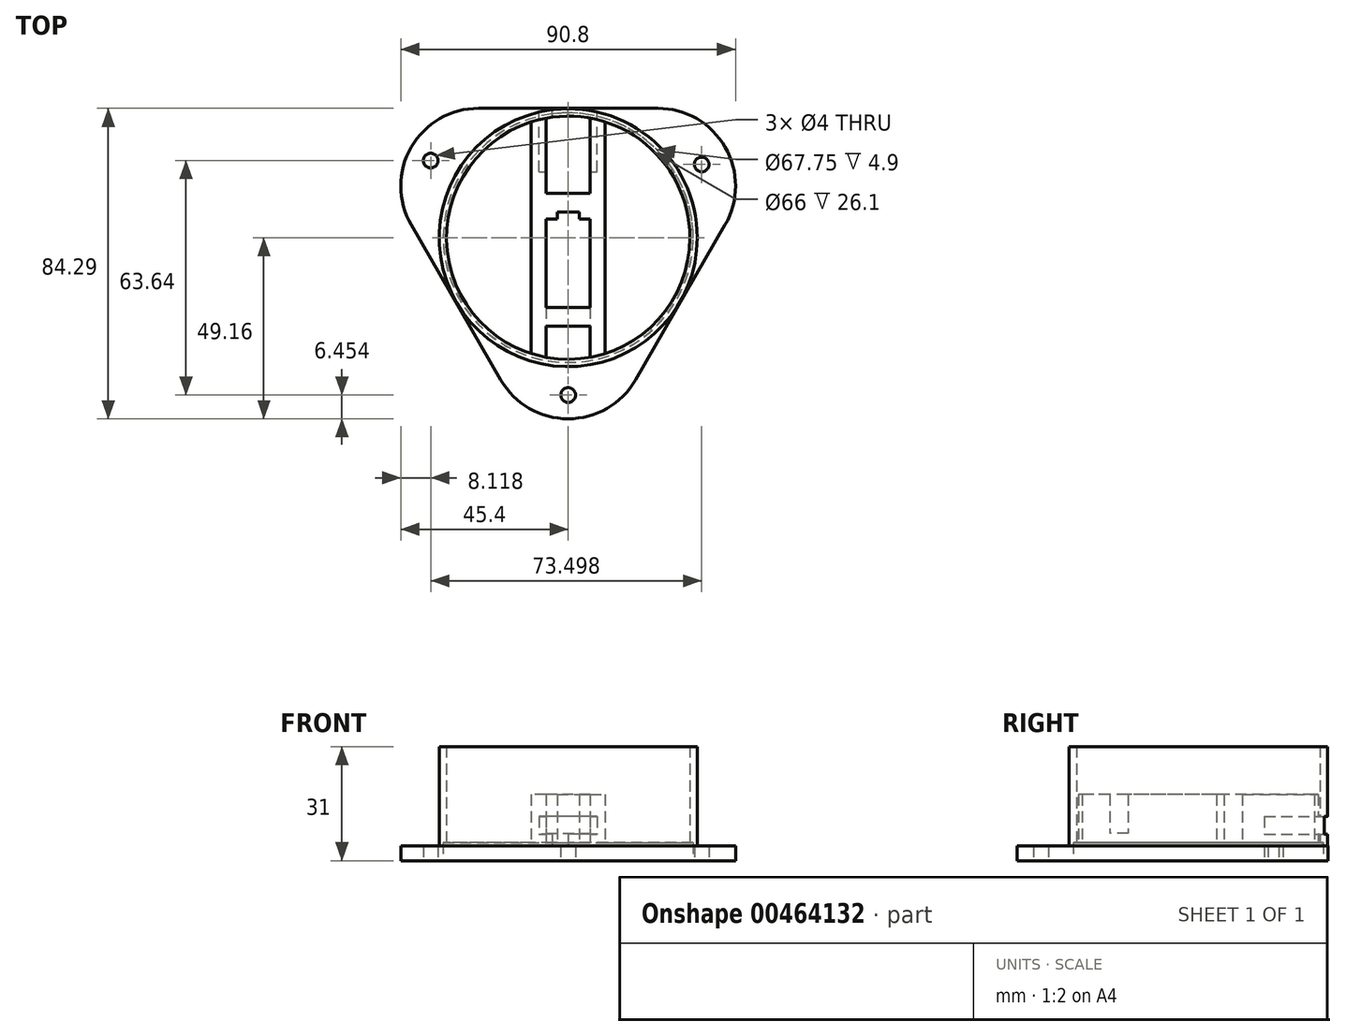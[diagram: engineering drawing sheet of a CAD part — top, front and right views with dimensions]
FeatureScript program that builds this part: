
annotation { "Feature Type Name" : "Feature", "Feature Type Description" : "" }
export const myFeature = defineFeature(function(context is Context, id is Id, definition is map)
    precondition{}
    {
        {
            var Q0;
            Q0=qCreatedBy(makeId("Top.planeOp"),FACE);
            var sketch = newSketch(context, id + "F0", { "sketchPlane" : qUnion([Q0])});
            skCircle(sketch, "E0", {"center": v(0, 0) * mm, "radius": 35 * mm});
            skCircle(sketch, "E1", {"center": v(0, 0) * mm, "radius": 33 * mm});
            skSolve(sketch);
        }
        {
            var Q0;
            Q0=qCreatedBy(makeId("Top.planeOp"),FACE);
            var sketch = newSketch(context, id + "F1", { "sketchPlane" : qUnion([Q0])});
            skPoint(sketch, "E2", {"position": v(0, -24) * mm});
            skPoint(sketch, "E3", {"position": v(0, -19) * mm});
            skPoint(sketch, "E4", {"position": v(6, -19) * mm});
            skPoint(sketch, "E5", {"position": v(-6, -19) * mm});
            skPoint(sketch, "E6", {"position": v(6, -24) * mm});
            skPoint(sketch, "E7", {"position": v(-6, -24) * mm});
            skPoint(sketch, "E8", {"position": v(10, -24) * mm});
            skLineSegment(sketch, "E9", {"start": v(10, -24) * mm, "end": v(10, -32.05) * mm});
            skLineSegment(sketch, "E10", {"start": v(6, -24) * mm, "end": v(6, -33.1) * mm});
            skPoint(sketch, "E11", {"position": v(6, 5) * mm});
            skPoint(sketch, "E12", {"position": v(3, 5) * mm});
            skPoint(sketch, "E13", {"position": v(3, 7) * mm});
            skPoint(sketch, "E14", {"position": v(3, 12) * mm});
            skPoint(sketch, "E15", {"position": v(6, 12) * mm});
            skPoint(sketch, "E16", {"position": v(10, 5) * mm});
            skPoint(sketch, "E17", {"position": v(10, 12) * mm});
            skLineSegment(sketch, "E18", {"start": v(10, -24) * mm, "end": v(10, 32.28) * mm});
            skLineSegment(sketch, "E19", {"start": v(6, 12) * mm, "end": v(6, 33.47) * mm});
            skLineSegment(sketch, "E20", {"start": v(6, 12) * mm, "end": v(3, 12) * mm});
            skLineSegment(sketch, "E21", {"start": v(3, 7) * mm, "end": v(3, 5) * mm});
            skLineSegment(sketch, "E22", {"start": v(3, 5) * mm, "end": v(6, 5) * mm});
            skLineSegment(sketch, "E23", {"start": v(6, 5) * mm, "end": v(6, -19) * mm});
            skPoint(sketch, "E24", {"position": v(0, 7) * mm});
            skPoint(sketch, "E25", {"position": v(0, 12) * mm});
            skLineSegment(sketch, "E26", {"start": v(3, 7) * mm, "end": v(0, 7) * mm});
            skLineSegment(sketch, "E27", {"start": v(3, 12) * mm, "end": v(0, 12) * mm});
            skLineSegment(sketch, "E28", {"start": v(0, -24) * mm, "end": v(6, -24) * mm});
            skLineSegment(sketch, "E29", {"start": v(0, -19) * mm, "end": v(6, -19) * mm});
            skLineSegment(sketch, "E30.MirrorCS", {"start": v(-3, 12) * mm, "end": v(0, 12) * mm});
            skLineSegment(sketch, "E31.MirrorCS", {"start": v(-6, 12) * mm, "end": v(-3, 12) * mm});
            skLineSegment(sketch, "E32.MirrorCS", {"start": v(-6, 12) * mm, "end": v(-6, 33.47) * mm});
            skLineSegment(sketch, "E33.MirrorCS", {"start": v(-10, -24) * mm, "end": v(-10, 32.28) * mm});
            skLineSegment(sketch, "E34.MirrorCS", {"start": v(-6, 5) * mm, "end": v(-6, -19) * mm});
            skLineSegment(sketch, "E35.MirrorCS", {"start": v(-3, 5) * mm, "end": v(-6, 5) * mm});
            skLineSegment(sketch, "E36.MirrorCS", {"start": v(-3, 7) * mm, "end": v(-3, 5) * mm});
            skLineSegment(sketch, "E37.MirrorCS", {"start": v(-3, 7) * mm, "end": v(0, 7) * mm});
            skLineSegment(sketch, "E38.MirrorCS", {"start": v(0, -19) * mm, "end": v(-6, -19) * mm});
            skLineSegment(sketch, "E39.MirrorCS", {"start": v(0, -24) * mm, "end": v(-6, -24) * mm});
            skLineSegment(sketch, "E40.MirrorCS", {"start": v(-6, -24) * mm, "end": v(-6, -33.1) * mm});
            skLineSegment(sketch, "E41.MirrorCS", {"start": v(-10, -24) * mm, "end": v(-10, -32.05) * mm});
            skLineSegment(sketch, "E42", {"start": v(6, 33.47) * mm, "end": v(10, 32.28) * mm});
            skLineSegment(sketch, "E43", {"start": v(-6, 33.47) * mm, "end": v(-10, 32.28) * mm});
            skLineSegment(sketch, "E44", {"start": v(-10, -32.05) * mm, "end": v(-6, -33.1) * mm});
            skLineSegment(sketch, "E45", {"start": v(6, -33.1) * mm, "end": v(10, -32.05) * mm});
            skSolve(sketch);
        }
        {
            var Q0;
            Q0=makeQuery(id+"F0.imprint","IMPRINT",FACE,{"disambiguationData":[TD([[makeQuery(id+"F0.imprint","IMPRINT",EDGE,{"derivedFrom":sQuery(id+"F0.wireOp",EDGE,"E0")}),1.0]])]});
            extrude(context, id + "F2", {"entities" : qUnion([Q0]), "depth" : 31 * mm});
        }
        {
            var Q0;
            Q0=makeQuery(id+"F1.imprint","IMPRINT",FACE,{"disambiguationData":[TD([[makeQuery(id+"F1.imprint","IMPRINT",EDGE,{"derivedFrom":sQuery(id+"F1.wireOp",EDGE,"E9")}),-1.0]])]});
            extrude(context, id + "F3", {"entities" : qUnion([Q0]), "operationType" : NewBodyOperationType.ADD, "depth" : 18 * mm});
        }
        {
            var Q0;
            Q0=sQuery(id+"F1.wireOp",EDGE,"E28");
            var Q1;
            Q1=sQuery(id+"F1.wireOp",EDGE,"E39.MirrorCS");
            extrude(context, id + "F4", {"bodyType" : ToolBodyType.SURFACE, "surfaceEntities" : qUnion([Q0, Q1]), "depth" : 7.5 * mm});
        }
        {
            var Q0;
            Q0=makeQuery(id+"F4.opExtrude","SWEPT_FACE",FACE,{"disambiguationData":[OSD([sQuery(id+"F1.wireOp",EDGE,"E28"),sQuery(id+"F1.wireOp",EDGE,"E39.MirrorCS")])]});
            extrude(context, id + "F5", {"entities" : qUnion([Q0]), "operationType" : NewBodyOperationType.REMOVE, "oppositeDirection" : true, "depth" : 9.3 * mm});
        }
        {
            var Q0;
            Q0=qCreatedBy(makeId("Top.planeOp"),FACE);
            var sketch = newSketch(context, id + "F6", { "sketchPlane" : qUnion([Q0])});
            skCircle(sketch, "E46.cCircle", {"center": v(0, 0) * mm, "radius": 35.13 * mm, "construction": true});
            skLineSegment(sketch, "E46.0", {"start": v(-60.85, 35.13) * mm, "end": v(60.85, 35.13) * mm});
            skLineSegment(sketch, "E46.1", {"start": v(60.85, 35.13) * mm, "end": v(0, -70.26) * mm});
            skLineSegment(sketch, "E46.2", {"start": v(0, -70.26) * mm, "end": v(-60.85, 35.13) * mm});
            skPoint(sketch, "E46.0.midPoint", {"position": v(0, 35.13) * mm});
            skSolve(sketch);
        }
        {
            var Q0;
            Q0=makeQuery(id+"F6.imprint","IMPRINT",FACE,{"disambiguationData":[TD([[makeQuery(id+"F6.imprint","IMPRINT",EDGE,{"derivedFrom":sQuery(id+"F6.wireOp",EDGE,"E46.0")}),-1.0]])]});
            extrude(context, id + "F7", {"entities" : qUnion([Q0]), "operationType" : NewBodyOperationType.ADD, "depth" : 4 * mm});
        }
        {
            var Q0;
            Q0=makeQuery(id+"F7.opExtrude","SWEPT_EDGE",EDGE,{"disambiguationData":[OSD([sQuery(id+"F6.wireOp",EDGE,"E46.0"),sQuery(id+"F6.wireOp",EDGE,"E46.2")])]});
            var Q1;
            Q1=makeQuery(id+"F7.opExtrude","SWEPT_EDGE",EDGE,{"disambiguationData":[OSD([sQuery(id+"F6.wireOp",EDGE,"E46.0"),sQuery(id+"F6.wireOp",EDGE,"E46.1")])]});
            var Q2;
            Q2=makeQuery(id+"F7.opExtrude","SWEPT_EDGE",EDGE,{"disambiguationData":[OSD([sQuery(id+"F6.wireOp",EDGE,"E46.1"),sQuery(id+"F6.wireOp",EDGE,"E46.2")])]});
            fillet(context, id + "F8", {"entities" : qUnion([Q0, Q1, Q2]), "radius" : 21.1 * mm, "tangentPropagation" : true, "allowEdgeOverflow" : false});
        }
        {
            var Q0;
            Q0=qCreatedBy(makeId("Top.planeOp"),FACE);
            var sketch = newSketch(context, id + "F9", { "sketchPlane" : qUnion([Q0])});
            skCircle(sketch, "E47", {"center": v(-37.28, 20.93) * mm, "radius": 2 * mm});
            skCircle(sketch, "E48", {"center": v(0, -42.7) * mm, "radius": 2 * mm});
            skCircle(sketch, "E49", {"center": v(36.22, 19.89) * mm, "radius": 2 * mm});
            skSolve(sketch);
        }
        {
            var Q0;
            Q0=qSketchRegion(id+"F9",true);
            extrude(context, id + "F10", {"entities" : qUnion([Q0]), "operationType" : NewBodyOperationType.REMOVE, "oppositeDirection" : true, "depth" : 38 * mm});
        }
        {
            var Q0;
            Q0=makeQuery(id+"F9.imprint","IMPRINT",FACE,{"disambiguationData":[TD([[makeQuery(id+"F9.imprint","IMPRINT",EDGE,{"derivedFrom":sQuery(id+"F9.wireOp",EDGE,"E49")}),1.0]])]});
            extrude(context, id + "F11", {"entities" : qUnion([Q0]), "operationType" : NewBodyOperationType.REMOVE, "depth" : 52 * mm});
        }
        {
            var Q0;
            Q0=makeQuery(id+"F9.imprint","IMPRINT",FACE,{"disambiguationData":[TD([[makeQuery(id+"F9.imprint","IMPRINT",EDGE,{"derivedFrom":sQuery(id+"F9.wireOp",EDGE,"E47")}),1.0]])]});
            var Q1;
            Q1=makeQuery(id+"F9.imprint","IMPRINT",FACE,{"disambiguationData":[TD([[makeQuery(id+"F9.imprint","IMPRINT",EDGE,{"derivedFrom":sQuery(id+"F9.wireOp",EDGE,"E48")}),1.0]])]});
            extrude(context, id + "F12", {"entities" : qUnion([Q0, Q1]), "operationType" : NewBodyOperationType.REMOVE, "depth" : 37.9 * mm});
        }
        {
            var Q0;
            Q0=qCreatedBy(makeId("Top.planeOp"),FACE);
            var sketch = newSketch(context, id + "F13", { "sketchPlane" : qUnion([Q0])});
            skCircle(sketch, "E50", {"center": v(0, 0) * mm, "radius": 33.88 * mm});
            skSolve(sketch);
        }
        {
            var Q0;
            Q0=qSketchRegion(id+"F13",true);
            extrude(context, id + "F14", {"entities" : qUnion([Q0]), "operationType" : NewBodyOperationType.REMOVE, "depth" : 4.9 * mm});
        }
        {
            var Q0;
            Q0=makeQuery(id+"F7.opExtrude","SWEPT_FACE",FACE,{"disambiguationData":[OSD([sQuery(id+"F6.wireOp",EDGE,"E46.0")])]});
            var sketch = newSketch(context, id + "F15", { "sketchPlane" : qUnion([Q0])});
            skLineSegment(sketch, "E51", {"start": v(-2.22, 1.63) * mm, "end": v(0, 9.6) * mm});
            skLineSegment(sketch, "E52.bottom", {"start": v(7.87, 12) * mm, "end": v(-7.87, 12) * mm});
            skLineSegment(sketch, "E52.top", {"start": v(7.87, 7.19) * mm, "end": v(-7.87, 7.19) * mm});
            skLineSegment(sketch, "E52.left", {"start": v(7.87, 12) * mm, "end": v(7.87, 7.19) * mm});
            skLineSegment(sketch, "E52.right", {"start": v(-7.87, 12) * mm, "end": v(-7.87, 7.19) * mm});
            skPoint(sketch, "E52.middle", {"position": v(0, 9.6) * mm});
            skLineSegment(sketch, "E53.bottom", {"start": v(4.3, 4) * mm, "end": v(0, 4) * mm});
            skLineSegment(sketch, "E53.top", {"start": v(4.3, 10.38) * mm, "end": v(0, 10.38) * mm});
            skLineSegment(sketch, "E53.left", {"start": v(4.3, 4) * mm, "end": v(4.3, 10.38) * mm});
            skLineSegment(sketch, "E53.right", {"start": v(0, 4) * mm, "end": v(0, 10.38) * mm});
            skPoint(sketch, "E53.middle", {"position": v(2.15, 7.19) * mm});
            skSolve(sketch);
        }
        {
            var Q0;
            Q0=makeQuery(id+"F15.imprint","IMPRINT",FACE,{"disambiguationData":[TD([[makeQuery(id+"F15.imprint","IMPRINT",EDGE,{"derivedFrom":sQuery(id+"F15.wireOp",EDGE,"E52.bottom")}),1.0]])]});
            var Q1;
            {var subQ5=sQuery(id+"F15.wireOp",EDGE,"E53.top");Q1=makeQuery(id+"F15.imprint","IMPRINT",FACE,{"disambiguationData":[TD([[makeQuery(id+"F15.imprint","IMPRINT",EDGE,{"derivedFrom":subQ5}),1.0]])]});}
            var Q2;
            {var subQ5=sQuery(id+"F15.wireOp",EDGE,"E53.bottom");Q2=makeQuery(id+"F15.imprint","IMPRINT",FACE,{"disambiguationData":[TD([[makeQuery(id+"F15.imprint","IMPRINT",EDGE,{"derivedFrom":subQ5}),-1.0]])]});}
            extrude(context, id + "F16", {"entities" : qUnion([Q0, Q1, Q2]), "operationType" : NewBodyOperationType.REMOVE, "oppositeDirection" : true, "depth" : 17.2 * mm});
        }
    });
